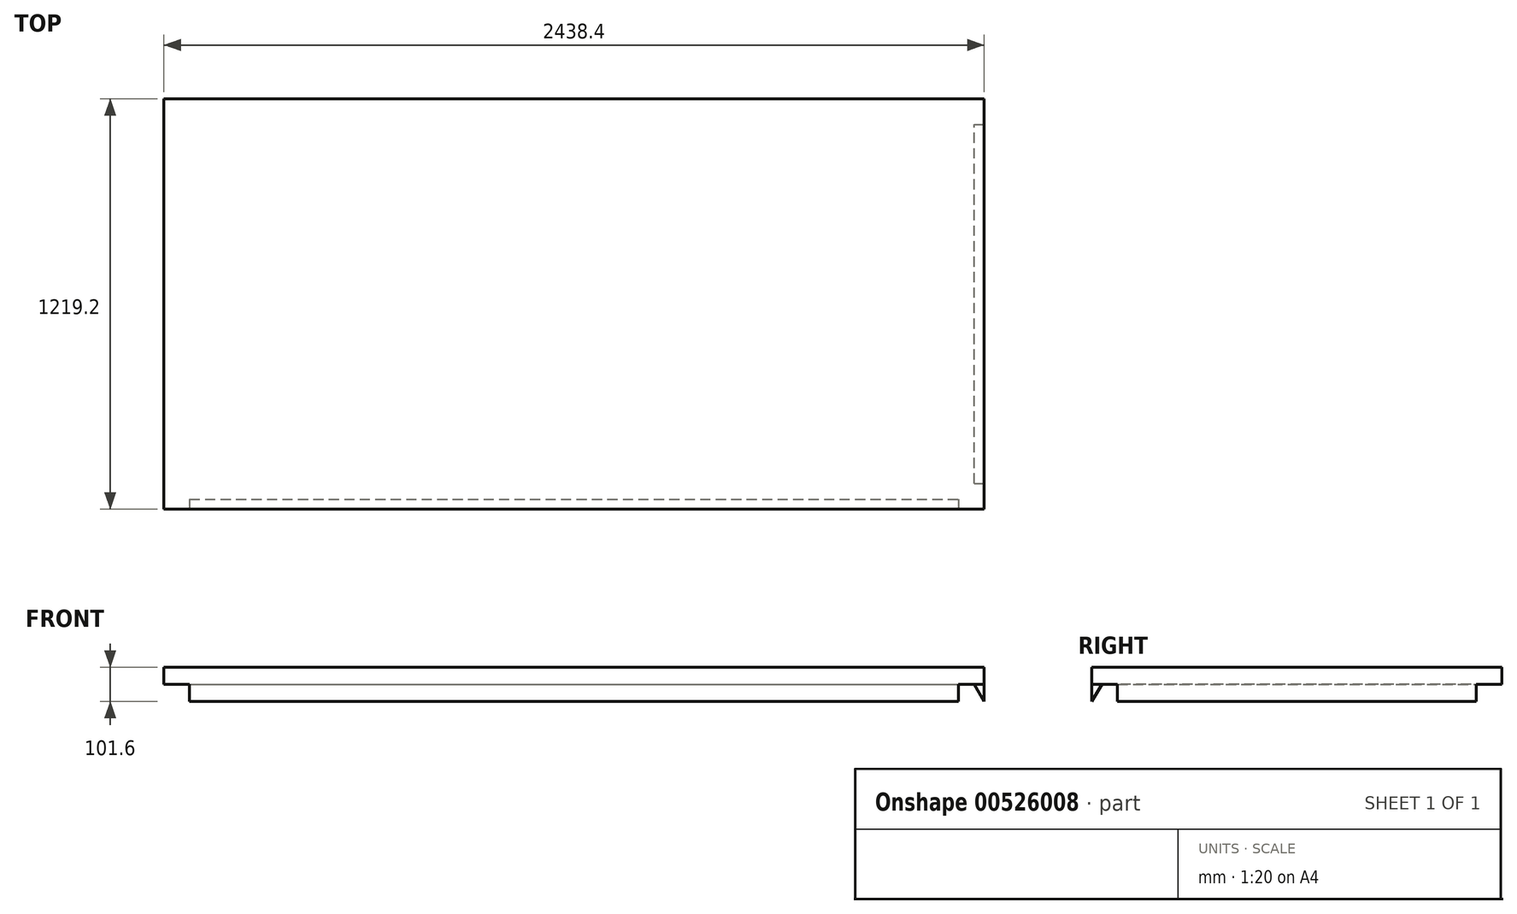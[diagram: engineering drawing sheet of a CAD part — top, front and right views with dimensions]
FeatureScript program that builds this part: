
annotation { "Feature Type Name" : "Feature", "Feature Type Description" : "" }
export const myFeature = defineFeature(function(context is Context, id is Id, definition is map)
    precondition{}
    {
        {
            var Q0;
            Q0=qCreatedBy(makeId("Top.planeOp"),FACE);
            var sketch = newSketch(context, id + "F0", { "sketchPlane" : qUnion([Q0])});
            skLineSegment(sketch, "E0.bottom", {"start": v(-1219.2, 609.6) * mm, "end": v(1219.2, 609.6) * mm});
            skLineSegment(sketch, "E0.top", {"start": v(-1219.2, -609.6) * mm, "end": v(1219.2, -609.6) * mm});
            skLineSegment(sketch, "E0.left", {"start": v(-1219.2, 609.6) * mm, "end": v(-1219.2, -609.6) * mm});
            skLineSegment(sketch, "E0.right", {"start": v(1219.2, 609.6) * mm, "end": v(1219.2, -609.6) * mm});
            skPoint(sketch, "E0.middle", {"position": v(0, 0) * mm});
            skSolve(sketch);
        }
        {
            var Q0;
            Q0=makeQuery(id+"F0.imprint","IMPRINT",FACE,{"disambiguationData":[TD([[makeQuery(id+"F0.imprint","IMPRINT",EDGE,{"derivedFrom":sQuery(id+"F0.wireOp",EDGE,"E0.bottom")}),-1.0]])]});
            extrude(context, id + "F1", {"entities" : qUnion([Q0]), "depth" : 50.8 * mm, "offsetDistance" : 25.4 * mm});
        }
        {
            var Q0;
            Q0=qCreatedBy(makeId("Right.planeOp"),FACE);
            var sketch = newSketch(context, id + "F2", { "sketchPlane" : qUnion([Q0])});
            skLineSegment(sketch, "E1", {"start": v(-580.27, 0) * mm, "end": v(-609.6, -50.8) * mm});
            skLineSegment(sketch, "E2", {"start": v(-609.6, 0) * mm, "end": v(-609.6, -50.8) * mm});
            skLineSegment(sketch, "E3.0", {"start": v(609.6, 0) * mm, "end": v(-609.6, 0) * mm});
            skSolve(sketch);
        }
        {
            var Q0;
            {var subQ0=sQuery(id+"F2.wireOp",EDGE,"E1");Q0=makeQuery(id+"F2.imprint","IMPRINT",FACE,{"disambiguationData":[TD([[makeQuery(id+"F2.imprint","IMPRINT",EDGE,{"derivedFrom":subQ0}),-1.0]])]});}
            extrude(context, id + "F3", {"entities" : qUnion([Q0]), "operationType" : NewBodyOperationType.ADD, "endBound" : BoundingType.SYMMETRIC, "oppositeDirection" : true, "depth" : 2286 * mm, "offsetDistance" : 25.4 * mm});
        }
        {
            var Q0;
            Q0=qCreatedBy(makeId("Front.planeOp"),FACE);
            cPlane(context, id + "F4", {"entities" : qUnion([Q0]), "cplaneType" : CPlaneType.OFFSET, "offset" : 0 * mm, "width" : 152.4 * mm, "height" : 152.4 * mm});
        }
        {
            var Q0;
            Q0=qCreatedBy(makeId("Front.planeOp"),FACE);
            var sketch = newSketch(context, id + "F5", { "sketchPlane" : qUnion([Q0])});
            skLineSegment(sketch, "E4.0", {"start": v(1143, 0) * mm, "end": v(1219.2, 0) * mm});
            skLineSegment(sketch, "E5", {"start": v(1219.2, 0) * mm, "end": v(1219.2, -50.8) * mm});
            skLineSegment(sketch, "E6", {"start": v(1219.2, -50.8) * mm, "end": v(1189.87, 0) * mm});
            skSolve(sketch);
        }
        {
            var Q0;
            {var subQ0=sQuery(id+"F5.wireOp",EDGE,"E5");Q0=makeQuery(id+"F5.imprint","IMPRINT",FACE,{"disambiguationData":[TD([[makeQuery(id+"F5.imprint","IMPRINT",EDGE,{"derivedFrom":subQ0}),-1.0]])]});}
            extrude(context, id + "F6", {"entities" : qUnion([Q0]), "operationType" : NewBodyOperationType.ADD, "endBound" : BoundingType.SYMMETRIC, "depth" : 1066.8 * mm, "offsetDistance" : 25.4 * mm});
        }
        {
            var Q0;
            Q0=qCreatedBy(makeId("Right.planeOp"),FACE);
            cPlane(context, id + "F7", {"entities" : qUnion([Q0]), "cplaneType" : CPlaneType.OFFSET, "offset" : 0 * mm, "width" : 152.4 * mm, "height" : 152.4 * mm});
        }
    });
